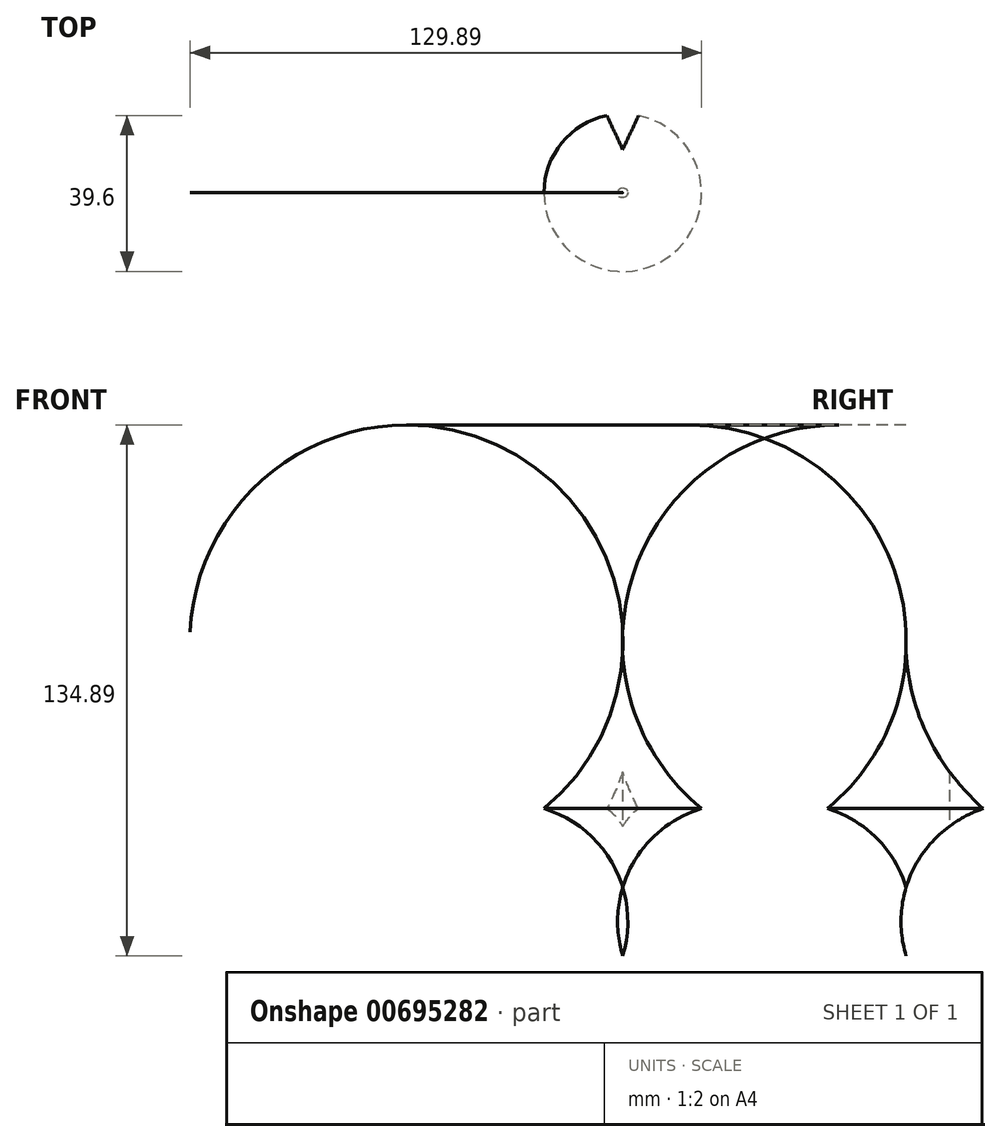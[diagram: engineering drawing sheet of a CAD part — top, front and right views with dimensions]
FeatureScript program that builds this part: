
annotation { "Feature Type Name" : "Feature", "Feature Type Description" : "" }
export const myFeature = defineFeature(function(context is Context, id is Id, definition is map)
    precondition{}
    {
        {
            var Q0;
            Q0=qCreatedBy(makeId("Front.planeOp"),FACE);
            var sketch = newSketch(context, id + "F0", { "sketchPlane" : qUnion([Q0])});
            skLineSegment(sketch, "E0", {"start": v(0, -45.21) * mm, "end": v(0, 73.71) * mm, "construction": true});
            skArc(sketch, "E1", {"start": v(20, 20) * mm, "mid": v(7.5, 12.5) * mm, "end": v(0, 0) * mm});
            skArc(sketch, "E2", {"start": v(0, 60) * mm, "mid": v(5.75, 37.88) * mm, "end": v(20, 20) * mm});
            skLineSegment(sketch, "E3", {"start": v(0, 60) * mm, "end": v(0, 0) * mm});
            skSolve(sketch);
        }
        {
            var Q0;
            Q0 = qSketchRegion(id + "F0", true);
            var Q1;
            Q1=sQuery(id+"F0.wireOp",EDGE,"E0");
            revolve(context, id + "F1", {"entities" : qUnion([Q0]), "axis" : qUnion([Q1]), "revolveType" : RevolveType.FULL});
        }
        {
            var Q0;
            Q0=qCreatedBy(makeId("Top.planeOp"),FACE);
            var sketch = newSketch(context, id + "F2", { "sketchPlane" : qUnion([Q0])});
            skCircle(sketch, "E4.0", {"center": v(0, 0) * mm, "radius": 20 * mm});
            skLineSegment(sketch, "E5", {"start": v(4, 19.6) * mm, "end": v(0, 11.02) * mm});
            skLineSegment(sketch, "E6", {"start": v(0, 11.02) * mm, "end": v(-4, 19.6) * mm});
            skLineSegment(sketch, "E7", {"start": v(0, 0) * mm, "end": v(0, 28.93) * mm, "construction": true});
            skLineSegment(sketch, "E8", {"start": v(0, 28.93) * mm, "end": v(23.1, 28.93) * mm, "construction": true});
            skSolve(sketch);
        }
        {
            var Q0;
            {var subQ0=sQuery(id+"F2.wireOp",EDGE,"E5");Q0=makeQuery(id+"F2.imprint","IMPRINT",FACE,{"disambiguationData":[TD([[makeQuery(id+"F2.imprint","IMPRINT",EDGE,{"derivedFrom":subQ0}),-1.0]])]});}
            extrude(context, id + "F3", {"entities" : qUnion([Q0]), "operationType" : NewBodyOperationType.REMOVE, "depth" : 33.4 * mm, "offsetDistance" : 25 * mm});
        }
    });
